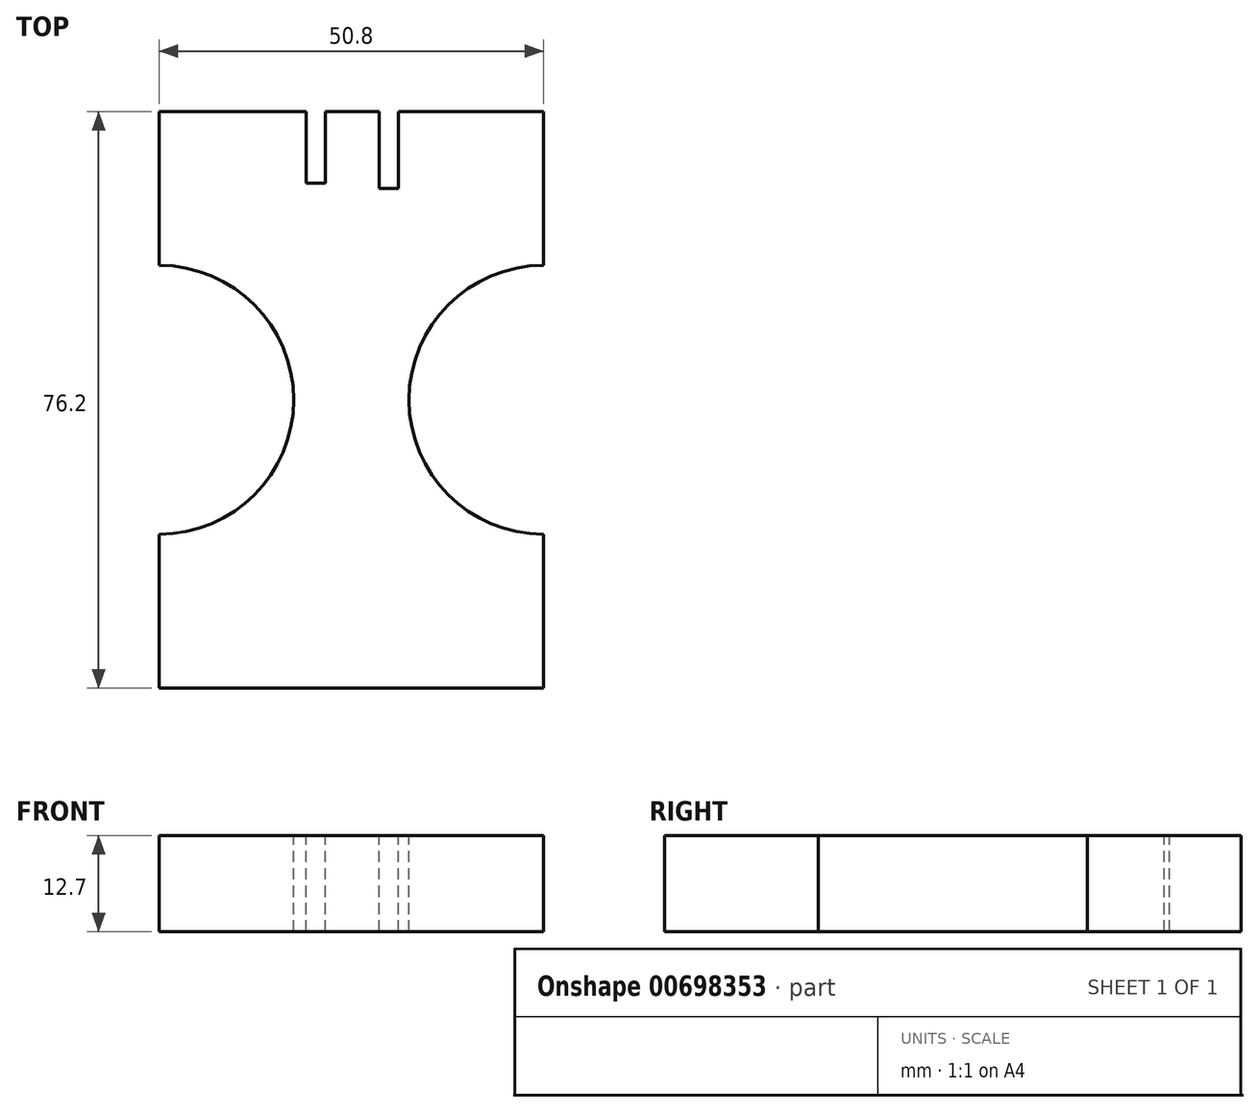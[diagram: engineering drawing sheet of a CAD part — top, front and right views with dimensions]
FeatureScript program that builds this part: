
annotation { "Feature Type Name" : "Feature", "Feature Type Description" : "" }
export const myFeature = defineFeature(function(context is Context, id is Id, definition is map)
    precondition{}
    {
        {
            var Q0;
            Q0=qCreatedBy(makeId("Top.planeOp"),FACE);
            var sketch = newSketch(context, id + "F0", { "sketchPlane" : qUnion([Q0])});
            skLineSegment(sketch, "E0.bottom", {"start": v(25.4, -38.1) * mm, "end": v(-25.4, -38.1) * mm});
            skLineSegment(sketch, "E0.top", {"start": v(25.4, 38.1) * mm, "end": v(-25.4, 38.1) * mm});
            skLineSegment(sketch, "E0.left", {"start": v(25.4, -38.1) * mm, "end": v(25.4, 38.1) * mm});
            skLineSegment(sketch, "E0.right", {"start": v(-25.4, -38.1) * mm, "end": v(-25.4, 38.1) * mm});
            skPoint(sketch, "E0.middle", {"position": v(0, 0) * mm});
            skSolve(sketch);
        }
        {
            var Q0;
            Q0 = qSketchRegion(id + "F0", true);
            extrude(context, id + "F1", {"entities" : qUnion([Q0]), "depth" : 12.7 * mm, "offsetDistance" : 25.4 * mm});
        }
        {
            var Q0;
            Q0=makeQuery(id+"F1.opExtrude","CAP_FACE",FACE,{"disambiguationData":[OSD([sQuery(id+"F0.wireOp",EDGE,"E0.bottom"),sQuery(id+"F0.wireOp",EDGE,"E0.top"),sQuery(id+"F0.wireOp",EDGE,"E0.left"),sQuery(id+"F0.wireOp",EDGE,"E0.right")])],"isStart":false});
            var sketch = newSketch(context, id + "F2", { "sketchPlane" : qUnion([Q0])});
            skCircle(sketch, "E1", {"center": v(25.4, 0) * mm, "radius": 17.78 * mm});
            skSolve(sketch);
        }
        {
            var Q0;
            Q0 = qSketchRegion(id + "F2", true);
            extrude(context, id + "F3", {"entities" : qUnion([Q0]), "operationType" : NewBodyOperationType.REMOVE, "oppositeDirection" : true, "depth" : 25.4 * mm, "offsetDistance" : 25.4 * mm});
        }
        {
            var Q0;
            Q0=makeQuery(id+"F1.opExtrude","CAP_FACE",FACE,{"disambiguationData":[OSD([sQuery(id+"F0.wireOp",EDGE,"E0.bottom"),sQuery(id+"F0.wireOp",EDGE,"E0.top"),sQuery(id+"F0.wireOp",EDGE,"E0.left"),sQuery(id+"F0.wireOp",EDGE,"E0.right")])],"isStart":false});
            var sketch = newSketch(context, id + "F4", { "sketchPlane" : qUnion([Q0])});
            skCircle(sketch, "E2", {"center": v(-25.4, 0) * mm, "radius": 17.78 * mm});
            skSolve(sketch);
        }
        {
            var Q0;
            Q0 = qSketchRegion(id + "F4", true);
            extrude(context, id + "F5", {"entities" : qUnion([Q0]), "operationType" : NewBodyOperationType.REMOVE, "oppositeDirection" : true, "depth" : 25.4 * mm, "offsetDistance" : 25.4 * mm});
        }
        {
            var Q0;
            Q0=makeQuery(id+"F1.opExtrude","CAP_FACE",FACE,{"disambiguationData":[OSD([sQuery(id+"F0.wireOp",EDGE,"E0.bottom"),sQuery(id+"F0.wireOp",EDGE,"E0.top"),sQuery(id+"F0.wireOp",EDGE,"E0.left"),sQuery(id+"F0.wireOp",EDGE,"E0.right")])],"isStart":false});
            var sketch = newSketch(context, id + "F6", { "sketchPlane" : qUnion([Q0])});
            skLineSegment(sketch, "E3.bottom", {"start": v(6.23, 38.1) * mm, "end": v(3.7, 38.1) * mm});
            skLineSegment(sketch, "E3.top", {"start": v(6.23, 27.94) * mm, "end": v(3.7, 27.94) * mm});
            skLineSegment(sketch, "E3.left", {"start": v(6.23, 38.1) * mm, "end": v(6.23, 27.94) * mm});
            skLineSegment(sketch, "E3.right", {"start": v(3.7, 38.1) * mm, "end": v(3.7, 27.94) * mm});
            skPoint(sketch, "E3.middle", {"position": v(4.96, 33.02) * mm});
            skSolve(sketch);
        }
        {
            var Q0;
            Q0 = qSketchRegion(id + "F6", true);
            extrude(context, id + "F7", {"entities" : qUnion([Q0]), "operationType" : NewBodyOperationType.REMOVE, "oppositeDirection" : true, "depth" : 25.4 * mm, "offsetDistance" : 25.4 * mm});
        }
        {
            var Q0;
            Q0=makeQuery(id+"F1.opExtrude","CAP_FACE",FACE,{"disambiguationData":[OSD([sQuery(id+"F0.wireOp",EDGE,"E0.bottom"),sQuery(id+"F0.wireOp",EDGE,"E0.top"),sQuery(id+"F0.wireOp",EDGE,"E0.left"),sQuery(id+"F0.wireOp",EDGE,"E0.right")])],"isStart":false});
            var sketch = newSketch(context, id + "F8", { "sketchPlane" : qUnion([Q0])});
            skLineSegment(sketch, "E4.bottom", {"start": v(-3.45, 28.67) * mm, "end": v(-5.99, 28.67) * mm});
            skLineSegment(sketch, "E4.top", {"start": v(-3.45, 38.83) * mm, "end": v(-5.99, 38.83) * mm});
            skLineSegment(sketch, "E4.left", {"start": v(-3.45, 28.67) * mm, "end": v(-3.45, 38.83) * mm});
            skLineSegment(sketch, "E4.right", {"start": v(-5.99, 28.67) * mm, "end": v(-5.99, 38.83) * mm});
            skPoint(sketch, "E4.middle", {"position": v(-4.72, 33.75) * mm});
            skSolve(sketch);
        }
        {
            var Q0;
            Q0 = qSketchRegion(id + "F8", true);
            extrude(context, id + "F9", {"entities" : qUnion([Q0]), "operationType" : NewBodyOperationType.REMOVE, "oppositeDirection" : true, "depth" : 25.4 * mm, "offsetDistance" : 25.4 * mm});
        }
    });
